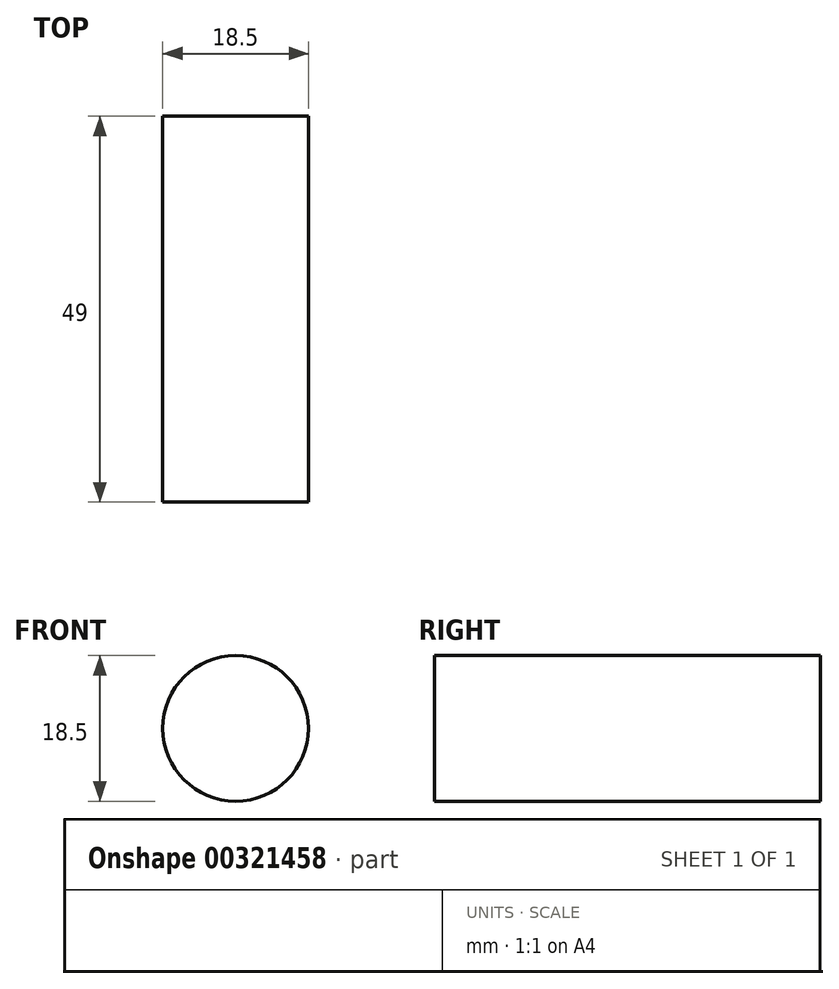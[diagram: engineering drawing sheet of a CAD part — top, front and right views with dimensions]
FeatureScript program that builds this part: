
annotation { "Feature Type Name" : "Feature", "Feature Type Description" : "" }
export const myFeature = defineFeature(function(context is Context, id is Id, definition is map)
    precondition{}
    {
        {
            var Q0;
            Q0=qCreatedBy(makeId("Front.planeOp"),FACE);
            var sketch = newSketch(context, id + "F0", { "sketchPlane" : qUnion([Q0])});
            skCircle(sketch, "E0", {"center": v(0, 0) * mm, "radius": 9.25 * mm});
            skSolve(sketch);
        }
        {
            var Q0;
            Q0 = qSketchRegion(id + "F0", true);
            extrude(context, id + "F1", {"entities" : qUnion([Q0]), "depth" : 49 * mm, "offsetDistance" : 25 * mm});
        }
    });
